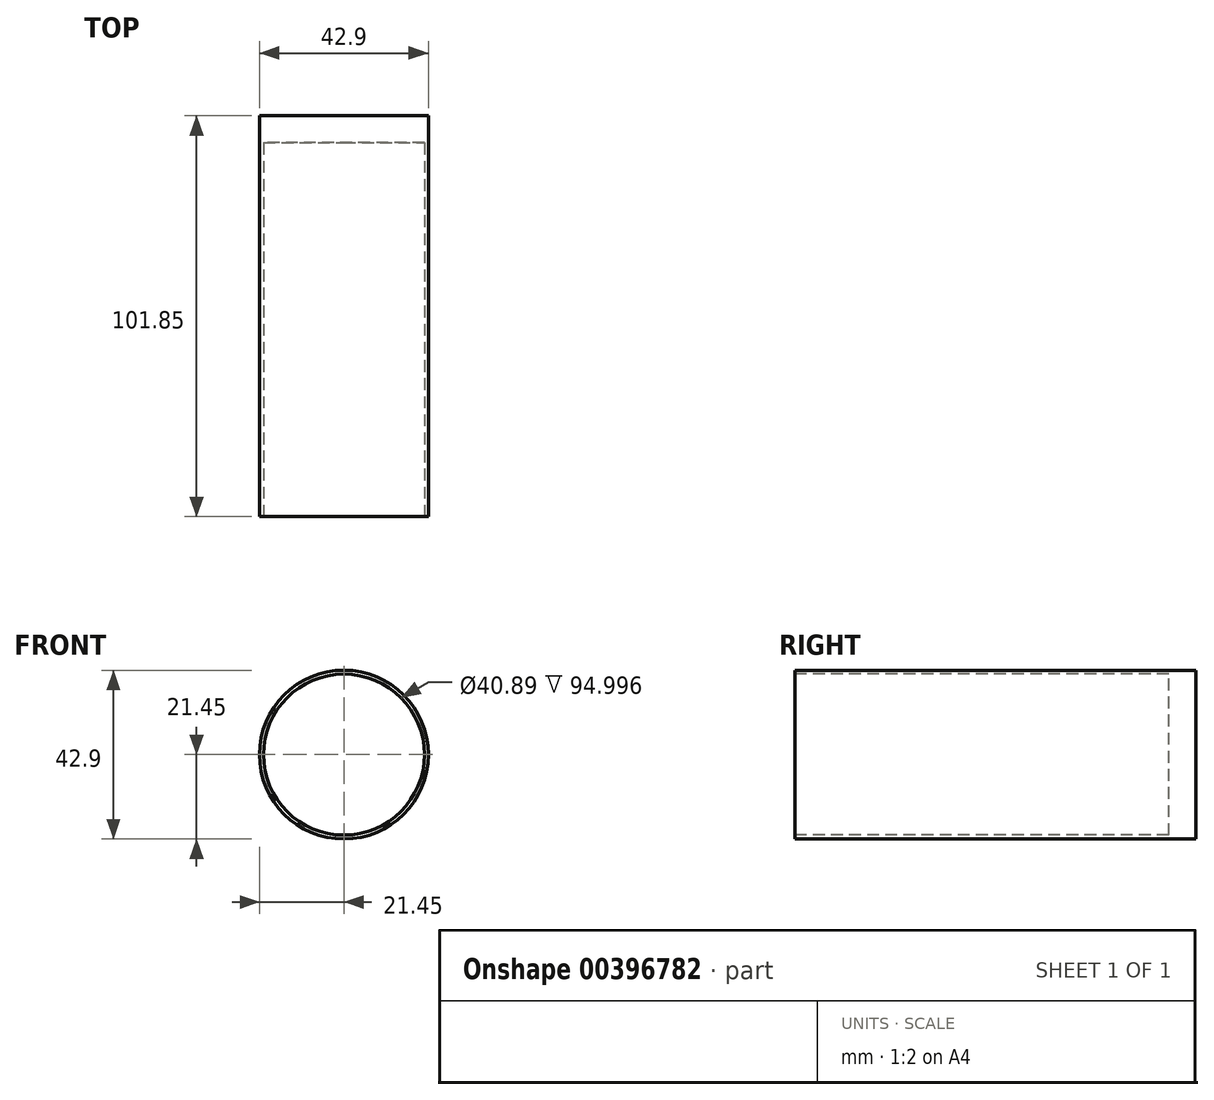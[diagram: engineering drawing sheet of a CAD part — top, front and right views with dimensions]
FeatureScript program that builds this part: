
annotation { "Feature Type Name" : "Feature", "Feature Type Description" : "" }
export const myFeature = defineFeature(function(context is Context, id is Id, definition is map)
    precondition{}
    {
        {
            var Q0;
            Q0=qCreatedBy(makeId("Front.planeOp"),FACE);
            var sketch = newSketch(context, id + "F0", { "sketchPlane" : qUnion([Q0])});
            skCircle(sketch, "E0", {"center": v(0, 0) * mm, "radius": 21.45 * mm});
            skSolve(sketch);
        }
        {
            var Q0;
            Q0 = qSketchRegion(id + "F0", true);
            extrude(context, id + "F1", {"entities" : qUnion([Q0]), "depth" : 101.85 * mm});
        }
        {
            var Q0;
            Q0=makeQuery(id+"F1.opExtrude","CAP_FACE",FACE,{"disambiguationData":[OSD([sQuery(id+"F0.wireOp",EDGE,"E0")])],"isStart":false});
            var sketch = newSketch(context, id + "F2", { "sketchPlane" : qUnion([Q0])});
            skCircle(sketch, "E1", {"center": v(0, 0) * mm, "radius": 20.44 * mm});
            skSolve(sketch);
        }
        {
            var Q0;
            Q0=makeQuery(id+"F2.imprint","IMPRINT",FACE,{"disambiguationData":[TD([[makeQuery(id+"F2.imprint","IMPRINT",EDGE,{"derivedFrom":sQuery(id+"F2.wireOp",EDGE,"E1")}),1.0]])]});
            var Q1;
            Q1=makeQuery(id+"F1.opExtrude","CAP_FACE",FACE,{"disambiguationData":[OSD([sQuery(id+"F0.wireOp",EDGE,"E0")])],"isStart":true});
            extrude(context, id + "F3", {"entities" : qUnion([Q0, Q1]), "operationType" : NewBodyOperationType.REMOVE, "oppositeDirection" : true, "depth" : 95 * mm});
        }
    });
